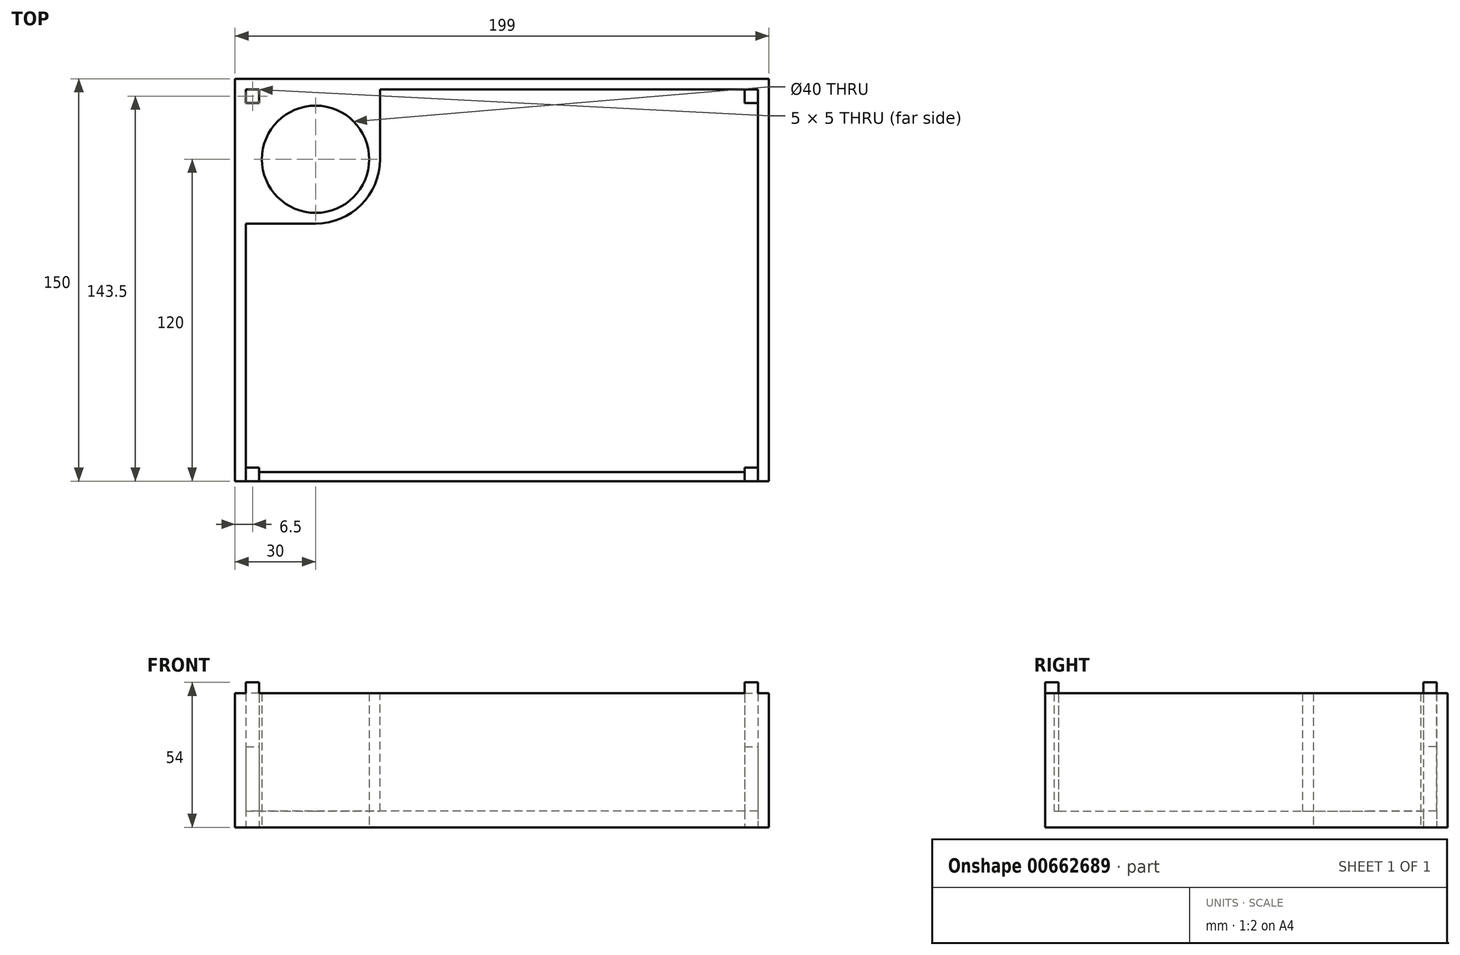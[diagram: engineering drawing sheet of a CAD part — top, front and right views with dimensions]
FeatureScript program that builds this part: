
annotation { "Feature Type Name" : "Feature", "Feature Type Description" : "" }
export const myFeature = defineFeature(function(context is Context, id is Id, definition is map)
    precondition{}
    {
        {
            var Q0;
            Q0=qCreatedBy(makeId("Top.planeOp"),FACE);
            cPlane(context, id + "F0", {"entities" : qUnion([Q0]), "cplaneType" : CPlaneType.OFFSET, "offset" : 30 * mm, "width" : 150 * mm, "height" : 150 * mm});
        }
        {
            var Q0;
            Q0=qCreatedBy(makeId("Top.planeOp"),FACE);
            var sketch = newSketch(context, id + "F1", { "sketchPlane" : qUnion([Q0])});
            skLineSegment(sketch, "E0.bottom", {"start": v(-99.5, 75) * mm, "end": v(99.5, 75) * mm});
            skLineSegment(sketch, "E0.left", {"start": v(-99.5, 75) * mm, "end": v(-99.5, -75) * mm});
            skLineSegment(sketch, "E0.right", {"start": v(99.5, 75) * mm, "end": v(99.5, -75) * mm});
            skPoint(sketch, "E0.middle", {"position": v(0, 0) * mm});
            skLineSegment(sketch, "E1.1", {"start": v(-95.5, 71) * mm, "end": v(-95.5, -70) * mm});
            skLineSegment(sketch, "E1.2", {"start": v(-95.5, 71) * mm, "end": v(95.4, 71) * mm});
            skLineSegment(sketch, "E1.3", {"start": v(95.4, 71) * mm, "end": v(95.4, -70) * mm});
            skLineSegment(sketch, "E2", {"start": v(0, -75) * mm, "end": v(0, -73) * mm});
            skPoint(sketch, "E2.endSnap0", {"position": v(0, -75) * mm});
            skPoint(sketch, "E3.end.orphan", {"position": v(95.5, 0) * mm});
            skLineSegment(sketch, "E4", {"start": v(-99.5, -75) * mm, "end": v(-95.5, -75) * mm});
            skLineSegment(sketch, "E5", {"start": v(-95.5, -75) * mm, "end": v(-95.5, -70) * mm});
            skLineSegment(sketch, "E6", {"start": v(95.4, -70) * mm, "end": v(95.4, -75) * mm});
            skLineSegment(sketch, "E7", {"start": v(95.4, -75) * mm, "end": v(99.5, -75) * mm});
            skPoint(sketch, "E8.end.orphan", {"position": v(-95.5, -70) * mm});
            skLineSegment(sketch, "E9", {"start": v(-90.5, 71) * mm, "end": v(-90.5, 66) * mm});
            skLineSegment(sketch, "E10", {"start": v(-90.5, 66) * mm, "end": v(-95.5, 66) * mm});
            skLineSegment(sketch, "E11", {"start": v(95.4, 66) * mm, "end": v(90.4, 66) * mm});
            skLineSegment(sketch, "E12", {"start": v(90.4, 66) * mm, "end": v(90.4, 71) * mm});
            skLineSegment(sketch, "E13", {"start": v(-95.5, 71) * mm, "end": v(-90.5, 71) * mm});
            skLineSegment(sketch, "E14", {"start": v(-95.5, 71) * mm, "end": v(-95.5, 66) * mm});
            skLineSegment(sketch, "E15", {"start": v(90.4, 71) * mm, "end": v(95.4, 71) * mm});
            skLineSegment(sketch, "E16", {"start": v(95.4, 66) * mm, "end": v(95.4, 71) * mm});
            skLineSegment(sketch, "E17", {"start": v(95.4, -75) * mm, "end": v(90.4, -75) * mm});
            skLineSegment(sketch, "E18", {"start": v(90.4, -75) * mm, "end": v(90.4, -70) * mm});
            skLineSegment(sketch, "E19", {"start": v(90.4, -70) * mm, "end": v(95.4, -70) * mm});
            skLineSegment(sketch, "E20", {"start": v(-95.5, -70) * mm, "end": v(-90.5, -70) * mm});
            skLineSegment(sketch, "E21", {"start": v(-95.5, -75) * mm, "end": v(-90.5, -75) * mm});
            skLineSegment(sketch, "E22", {"start": v(-90.5, -70) * mm, "end": v(-90.5, -75) * mm});
            skLineSegment(sketch, "E23", {"start": v(0, 73) * mm, "end": v(0, 71) * mm});
            skPoint(sketch, "E24.MirrorCS.end.orphan", {"position": v(-8.62, 71) * mm});
            skPoint(sketch, "E24.MirrorCS.start.orphan", {"position": v(8.62, 71) * mm});
            skLineSegment(sketch, "E25", {"start": v(-90.5, -75) * mm, "end": v(90.4, -75) * mm});
            skLineSegment(sketch, "E26", {"start": v(-90.5, -71.58) * mm, "end": v(90.4, -71.58) * mm});
            skSolve(sketch);
        }
        {
            var Q0;
            Q0=qCreatedBy(makeId("Top.planeOp"),FACE);
            var sketch = newSketch(context, id + "F2", { "sketchPlane" : qUnion([Q0])});
            skLineSegment(sketch, "E27.bottom", {"start": v(-99.5, 75) * mm, "end": v(-20, 75) * mm});
            skLineSegment(sketch, "E27.top", {"start": v(-99.5, -75) * mm, "end": v(99.5, -75) * mm});
            skLineSegment(sketch, "E27.left", {"start": v(-99.5, 75) * mm, "end": v(-99.5, -75) * mm});
            skLineSegment(sketch, "E27.right", {"start": v(99.5, 75) * mm, "end": v(99.5, -75) * mm});
            skPoint(sketch, "E27.middle", {"position": v(0, 0) * mm});
            skCircle(sketch, "E28", {"center": v(-69.5, 45) * mm, "radius": 20 * mm});
            skLineSegment(sketch, "E29.trimOffspring", {"start": v(20, 75) * mm, "end": v(99.5, 75) * mm});
            skLineSegment(sketch, "E30", {"start": v(-20, 75) * mm, "end": v(20, 75) * mm});
            skCircle(sketch, "E31", {"center": v(-69.5, 45) * mm, "radius": 24 * mm});
            skLineSegment(sketch, "E32", {"start": v(-45.5, 45) * mm, "end": v(-45.5, 75) * mm});
            skLineSegment(sketch, "E33", {"start": v(-69.5, 21) * mm, "end": v(-99.5, 21) * mm});
            skSolve(sketch);
        }
        {
            var Q0;
            Q0=qSketchRegion(id+"F2",true);
            extrude(context, id + "F3", {"entities" : qUnion([Q0]), "depth" : 6 * mm, "offsetDistance" : 25 * mm});
        }
        {
            var Q0;
            Q0=qSketchRegion(id+"F1",true);
            extrude(context, id + "F4", {"entities" : qUnion([Q0]), "operationType" : NewBodyOperationType.ADD, "depth" : 50 * mm, "offsetDistance" : 25 * mm});
        }
        {
            var Q0;
            Q0=makeQuery(id+"F4.opExtrude","CAP_FACE",FACE,{"disambiguationData":[OSD([sQuery(id+"F1.wireOp",EDGE,"E0.bottom"),sQuery(id+"F1.wireOp",EDGE,"E0.left"),sQuery(id+"F1.wireOp",EDGE,"E0.right"),sQuery(id+"F1.wireOp",EDGE,"E1.1"),sQuery(id+"F1.wireOp",EDGE,"E1.2"),sQuery(id+"F1.wireOp",EDGE,"E1.3"),sQuery(id+"F1.wireOp",EDGE,"vHm2nZUs-zN3H-GiGX-lCQW-jJyR5Z1LCUo2"),sQuery(id+"F1.wireOp",EDGE,"8aDH8xKs-Gtt8-g8Oy-8LFi-XUooxv0xEbeL"),sQuery(id+"F1.wireOp",EDGE,"qPj1n8vf-XcSi-lL73-26WJ-7Jw6quZBB5sQ"),sQuery(id+"F1.wireOp",EDGE,"hNI3CT3k-oqQM-9dc0-m5WW-2sYubDtYBGtc"),sQuery(id+"F1.wireOp",EDGE,"E24.MirrorCS"),sQuery(id+"F1.wireOp",EDGE,"E4"),sQuery(id+"F1.wireOp",EDGE,"E6"),sQuery(id+"F1.wireOp",EDGE,"E7"),sQuery(id+"F1.wireOp",EDGE,"z4k9ZTDm-Tq8Q-hJPG-9DCs-khOmU3JnDu57"),sQuery(id+"F1.wireOp",EDGE,"bnb6rr5d-InJ6-HeaA-qRYu-KReKVEHZzUvm"),sQuery(id+"F1.wireOp",EDGE,"E8"),sQuery(id+"F1.wireOp",EDGE,"4uPoHomk-Ry2O-OSnv-jVGb-2KsUEzkv8e3G"),sQuery(id+"F1.wireOp",EDGE,"I5YrnmAB-6gpW-rXWC-HDxQ-ym32sVAo6ccl"),sQuery(id+"F1.wireOp",EDGE,"SCJZ5amQ-SxxY-DkKT-6Xja-bVqgSrtH7FM3")])],"isStart":false});
            var sketch = newSketch(context, id + "F5", { "sketchPlane" : qUnion([Q0])});
            skSolve(sketch);
        }
        {
            var Q0;
            Q0=makeQuery(id+"F1.imprint","IMPRINT",FACE,{"disambiguationData":[TD([[makeQuery(id+"F1.imprint","IMPRINT",EDGE,{"derivedFrom":sQuery(id+"F1.wireOp",EDGE,"E9")}),-1.0]])]});
            extrude(context, id + "F6", {"entities" : qUnion([Q0]), "operationType" : NewBodyOperationType.ADD, "depth" : 54 * mm, "offsetDistance" : 25 * mm});
        }
        {
            var Q0;
            Q0=makeQuery(id+"F1.imprint","IMPRINT",FACE,{"disambiguationData":[TD([[makeQuery(id+"F1.imprint","IMPRINT",EDGE,{"derivedFrom":sQuery(id+"F1.wireOp",EDGE,"E11")}),-1.0]])]});
            var Q1;
            Q1=makeQuery(id+"F1.imprint","IMPRINT",FACE,{"disambiguationData":[TD([[makeQuery(id+"F1.imprint","IMPRINT",EDGE,{"derivedFrom":sQuery(id+"F1.wireOp",EDGE,"E6")}),-1.0]])]});
            var Q2;
            Q2=makeQuery(id+"F1.imprint","IMPRINT",FACE,{"disambiguationData":[TD([[makeQuery(id+"F1.imprint","IMPRINT",EDGE,{"derivedFrom":sQuery(id+"F1.wireOp",EDGE,"E5")}),-1.0]])]});
            extrude(context, id + "F7", {"entities" : qUnion([Q0, Q1, Q2]), "operationType" : NewBodyOperationType.ADD, "depth" : 54 * mm, "offsetDistance" : 25 * mm});
        }
        {
            var Q0;
            Q0=makeQuery(id+"F2.imprint","IMPRINT",FACE,{"disambiguationData":[TD([[makeQuery(id+"F2.imprint","IMPRINT",EDGE,{"derivedFrom":sQuery(id+"F2.wireOp",EDGE,"E28")}),-1.0]])]});
            var Q1;
            {var subQ0=sQuery(id+"F2.wireOp",EDGE,"E32");Q1=makeQuery(id+"F2.imprint","IMPRINT",FACE,{"disambiguationData":[TD([[makeQuery(id+"F2.imprint","IMPRINT",EDGE,{"derivedFrom":subQ0}),1.0]])]});}
            extrude(context, id + "F8", {"entities" : qUnion([Q0, Q1]), "operationType" : NewBodyOperationType.ADD, "depth" : 50 * mm, "offsetDistance" : 25 * mm});
        }
        {
            var Q0;
            Q0=makeQuery(id+"F1.imprint","IMPRINT",FACE,{"disambiguationData":[TD([[makeQuery(id+"F1.imprint","IMPRINT",EDGE,{"derivedFrom":sQuery(id+"F1.wireOp",EDGE,"E1.1")}),1.0]])]});
            var Q1;
            Q1=makeQuery(id+"F1.imprint","IMPRINT",FACE,{"disambiguationData":[TD([[makeQuery(id+"F1.imprint","IMPRINT",EDGE,{"derivedFrom":sQuery(id+"F1.wireOp",EDGE,"E9")}),-1.0]])]});
            var Q2;
            Q2=makeQuery(id+"F1.imprint","IMPRINT",FACE,{"disambiguationData":[TD([[makeQuery(id+"F1.imprint","IMPRINT",EDGE,{"derivedFrom":sQuery(id+"F1.wireOp",EDGE,"E11")}),-1.0]])]});
            extrude(context, id + "F9", {"entities" : qUnion([Q0, Q1, Q2]), "operationType" : NewBodyOperationType.REMOVE, "depth" : 30 * mm, "offsetDistance" : 25 * mm});
        }
    });
